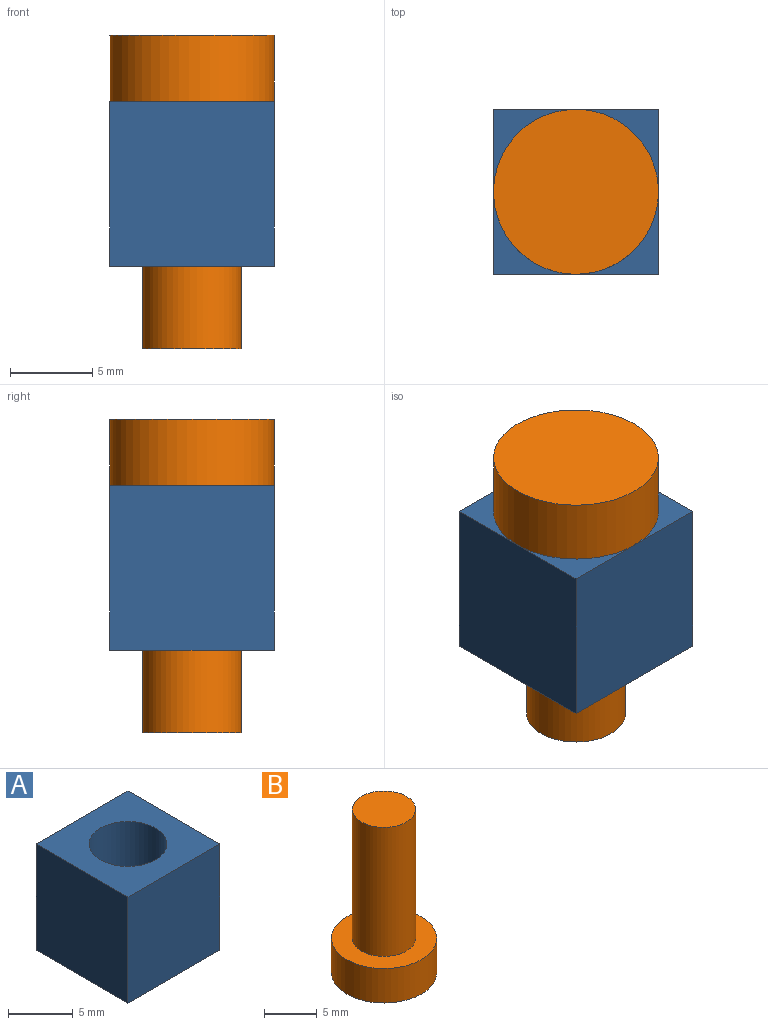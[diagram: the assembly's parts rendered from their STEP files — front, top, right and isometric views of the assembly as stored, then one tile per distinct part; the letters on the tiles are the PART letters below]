
ASSEMBLY  parts=2 mates=1
PART A: 7 faces, bbox 10x10x10 mm
  f0: plane 10x10mm, normal (0,1,0), area 100mm2, adj f1,f3,f4,f5
  f1: plane 10x10mm, normal (-1,0,0), area 100mm2, adj f0,f2,f4,f5
  f2: plane 10x10mm, normal (0,-1,0), area 100mm2, adj f1,f3,f4,f5
  f3: plane 10x10mm, normal (1,0,0), area 100mm2, adj f0,f2,f4,f5
  f4: plane 10x10mm, normal (0,0,1), area 71.7mm2, adj f0,f1,f2,f3,f6
  f5: plane 10x10mm, normal (0,0,-1), area 71.7mm2, adj f0,f1,f2,f3,f6
  f6: cylinder r=3mm len=10mm, axis (0,0,1), area 188.5mm2, adj f4,f5
PART B: 5 faces, bbox 10x10x19 mm
  f0: cylinder r=5mm len=10mm, axis (0,0,-1), area 125.7mm2, adj f1,f2
  f1: plane 10x10mm, normal (0,0,1), area 50.3mm2, adj f0,f3
  f2: plane 10x10mm, normal (0,0,-1), area 78.5mm2, adj f0
  f3: cylinder r=3mm len=15mm, axis (0,0,-1), area 282.7mm2, adj f1,f4
  f4: plane 6x6mm, normal (0,0,1), area 28.3mm2, adj f3
PLACE A at identity
PLACE B rot(axis=(1,0,0),180deg) t=(0,0,14)mm
MATE fastened B.f3 <-> A.f6  axis (0,0,1) through (0,0,10)mm
